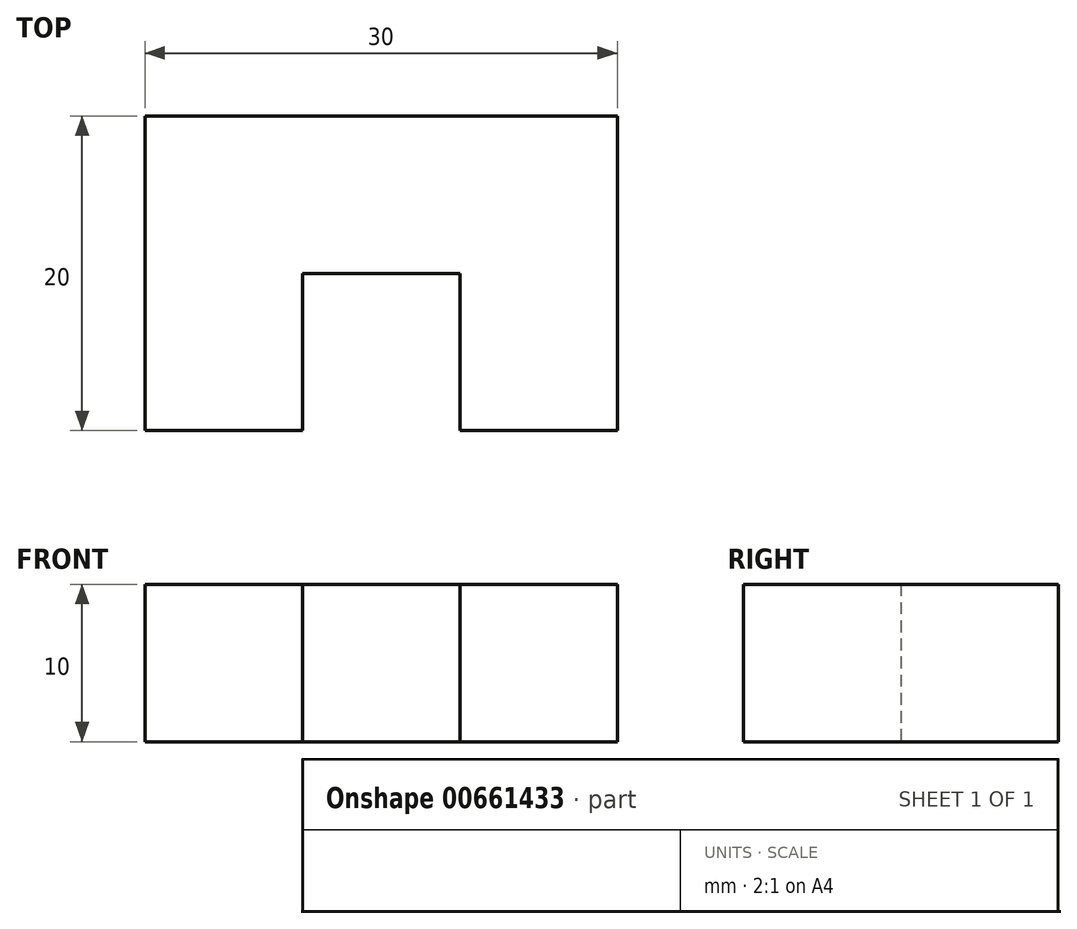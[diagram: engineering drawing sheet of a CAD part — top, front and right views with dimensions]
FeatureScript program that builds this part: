
annotation { "Feature Type Name" : "Feature", "Feature Type Description" : "" }
export const myFeature = defineFeature(function(context is Context, id is Id, definition is map)
    precondition{}
    {
        {
            var Q0;
            Q0=qCreatedBy(makeId("Top.planeOp"),FACE);
            var sketch = newSketch(context, id + "F0", { "sketchPlane" : qUnion([Q0])});
            skLineSegment(sketch, "E0", {"start": v(0, 0) * mm, "end": v(10, 0) * mm});
            skLineSegment(sketch, "E1", {"start": v(10, 0) * mm, "end": v(10, -10) * mm});
            skLineSegment(sketch, "E2", {"start": v(10, -10) * mm, "end": v(20, -10) * mm});
            skLineSegment(sketch, "E3", {"start": v(20, -10) * mm, "end": v(20, 10) * mm});
            skLineSegment(sketch, "E4", {"start": v(20, 10) * mm, "end": v(-10, 10) * mm});
            skLineSegment(sketch, "E5", {"start": v(-10, 10) * mm, "end": v(-10, -10) * mm});
            skLineSegment(sketch, "E6", {"start": v(-10, -10) * mm, "end": v(0, -10) * mm});
            skLineSegment(sketch, "E7", {"start": v(0, -10) * mm, "end": v(0, 0) * mm});
            skSolve(sketch);
        }
        {
            var Q0;
            Q0 = qSketchRegion(id + "F0", true);
            extrude(context, id + "F1", {"entities" : qUnion([Q0]), "depth" : 10 * mm, "offsetDistance" : 25 * mm});
        }
    });
